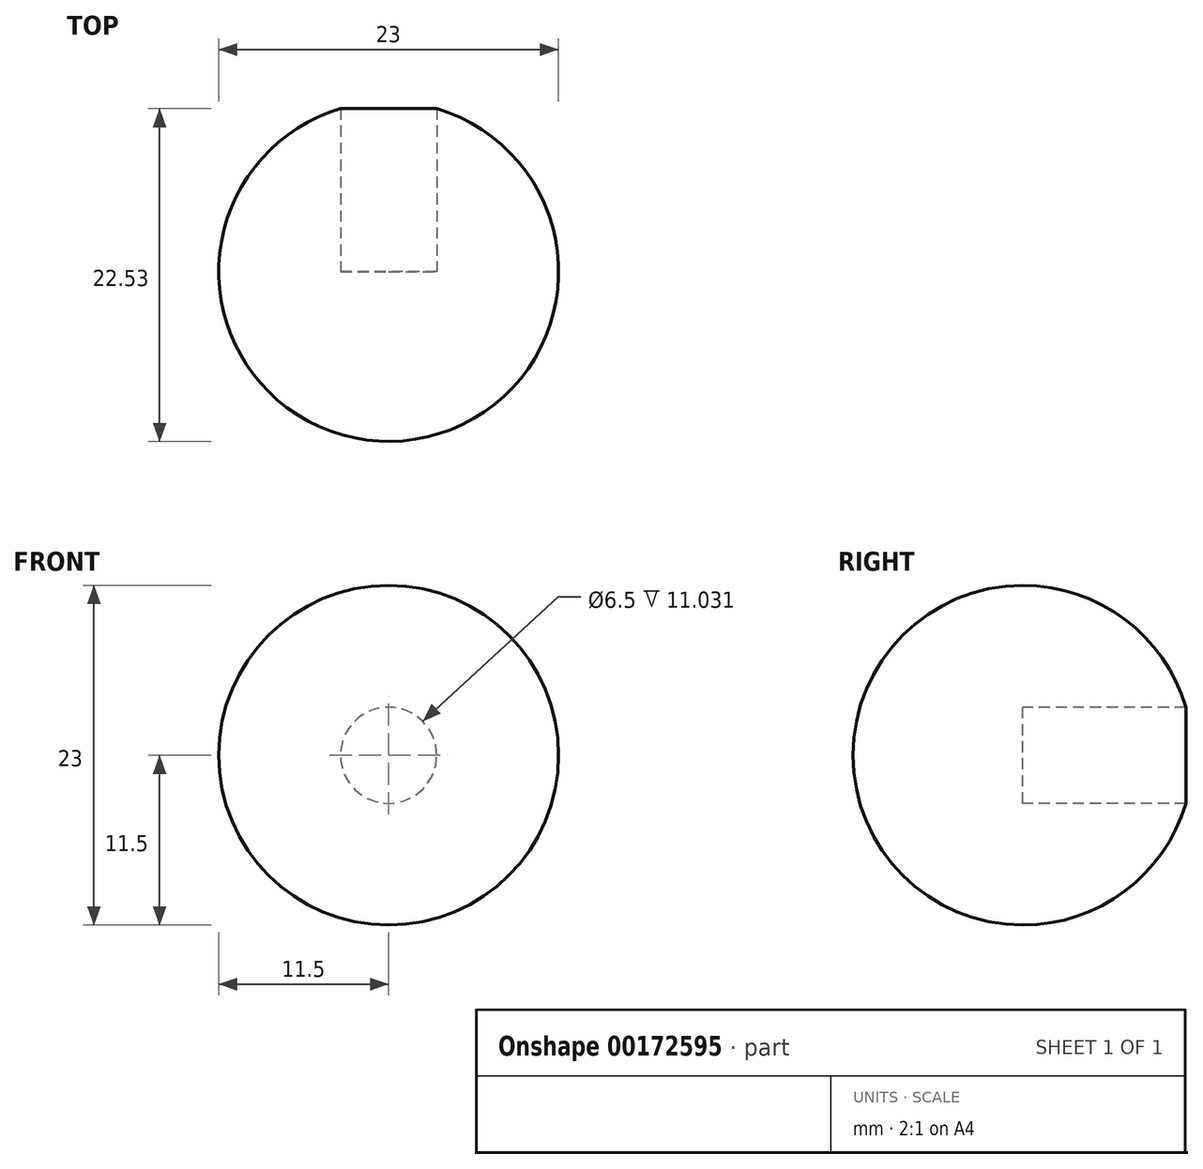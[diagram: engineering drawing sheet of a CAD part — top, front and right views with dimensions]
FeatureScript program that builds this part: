
annotation { "Feature Type Name" : "Feature", "Feature Type Description" : "" }
export const myFeature = defineFeature(function(context is Context, id is Id, definition is map)
    precondition{}
    {
        {
            var Q0;
            Q0=qCreatedBy(makeId("Front.planeOp"),FACE);
            var sketch = newSketch(context, id + "F0", { "sketchPlane" : qUnion([Q0])});
            skArc(sketch, "E0", {"start": v(0, 11.5) * mm, "mid": v(-11.5, 0) * mm, "end": v(0, -11.5) * mm});
            skLineSegment(sketch, "E1", {"start": v(0, 11.5) * mm, "end": v(0, -11.5) * mm});
            skSolve(sketch);
        }
        {
            var Q0;
            Q0=makeQuery(id+"F0.imprint","IMPRINT",FACE,{"disambiguationData":[TD([[makeQuery(id+"F0.imprint","IMPRINT",EDGE,{"derivedFrom":sQuery(id+"F0.wireOp",EDGE,"E0")}),1.0]])]});
            var Q1;
            Q1=sQuery(id+"F0.wireOp",EDGE,"E1");
            revolve(context, id + "F1", {"entities" : qUnion([Q0]), "axis" : qUnion([Q1]), "revolveType" : RevolveType.FULL});
        }
        {
            var Q0;
            Q0=qCreatedBy(makeId("Front.planeOp"),FACE);
            var sketch = newSketch(context, id + "F2", { "sketchPlane" : qUnion([Q0])});
            skCircle(sketch, "E2", {"center": v(0, 0) * mm, "radius": 3.25 * mm});
            skSolve(sketch);
        }
        {
            var Q0;
            Q0=sQuery(id+"F2.wireOp",VERTEX,"E2.center");
            var Q1;
            Q1=makeQuery(id+"F1.opRevolve","SWEPT_BODY",BODY,{"disambiguationData":[OSD([sQuery(id+"F0.wireOp",EDGE,"E0"),sQuery(id+"F0.wireOp",EDGE,"E1")])]});
            hole(context, id + "F3", {"style" : HoleStyle.SIMPLE, "endStyle" : HoleEndStyle.BLIND, "holeDiameter" : 6.5 * mm, "holeDepth" : 11.5 * mm, "startFromSketch" : true, "locations" : qUnion([Q0]), "scope" : qUnion([Q1])});
        }
    });
